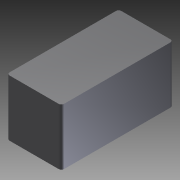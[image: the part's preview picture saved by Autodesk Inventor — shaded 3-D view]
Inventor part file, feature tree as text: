
AUTODESK INVENTOR PART (.ipt)
format: ipt  version: 2015 (Build 190159000, 159)  size: 82,432 bytes
history: native  units: in
note: dims shown in document units (in); Inventor stores cm internally (conversion verified against a paired STEP export)
features: fillet x1, other x1, imported_body x1
ambient origin geometry x8: Origin, YZ Plane, XZ Plane, XY Plane, X Axis, Y Axis, Z Axis, Center Point
bodies: Body1 (feature_tree)
feature tree (3):
  fillet  "Fillet1"  [1 undecoded]
  other  "TOWER PRO MG-995, ANALOG SERVO, BODY, MIDDLE.ipt1"
  imported_body  "Base1"
note: 1 required parameter value undecoded (feature->parameter linkage not recoverable at this tier; creation-order binding heuristic only, values carry confidence <= 0.55)
